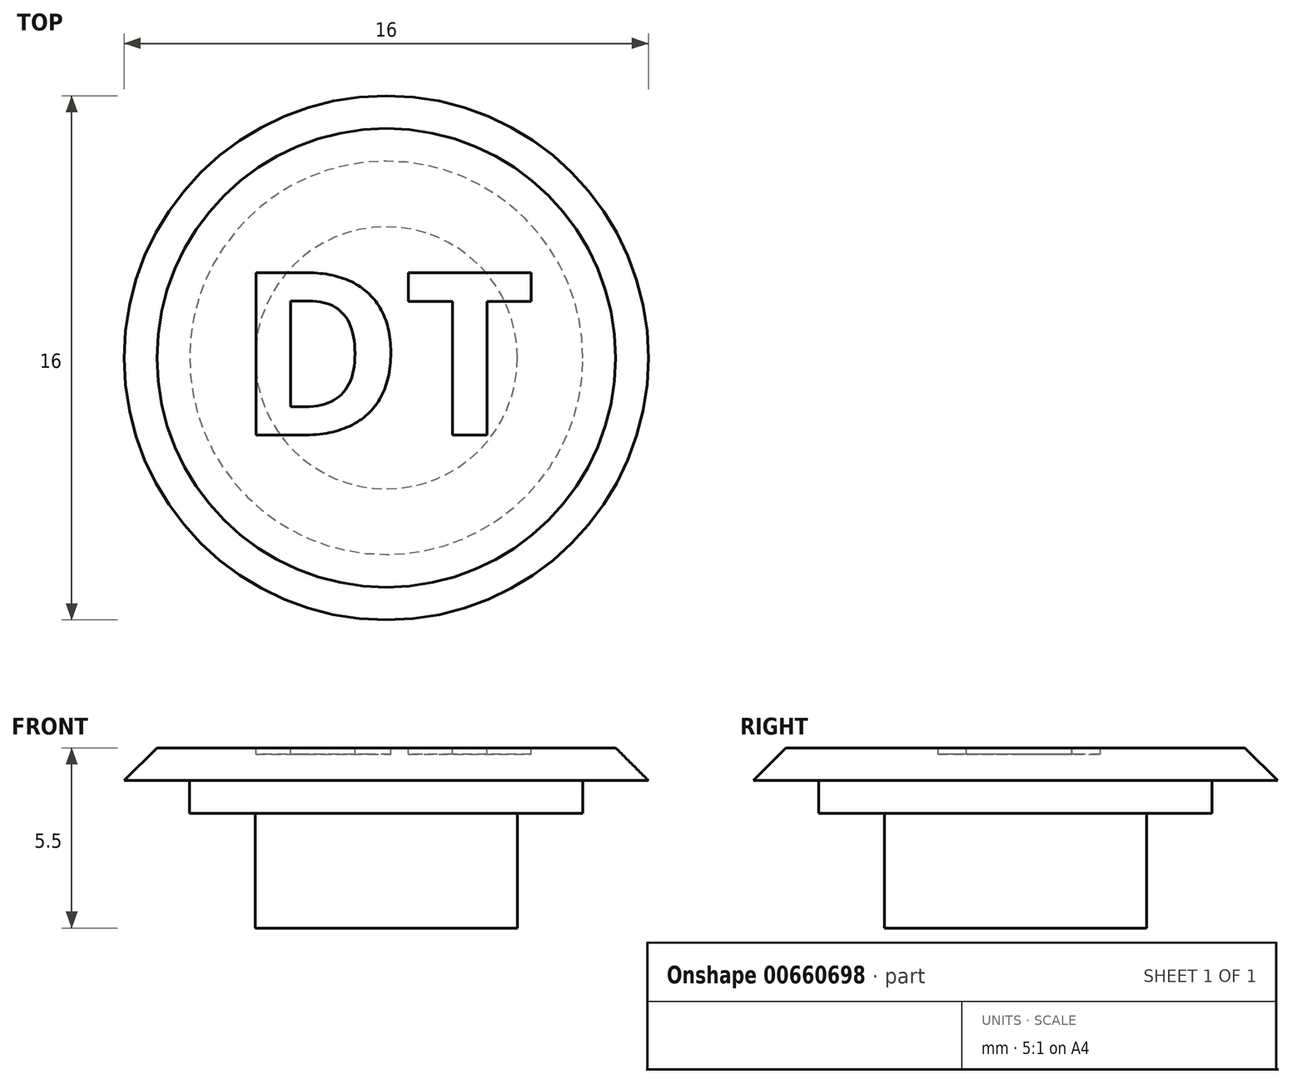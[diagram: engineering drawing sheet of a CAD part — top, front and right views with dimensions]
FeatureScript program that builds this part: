
annotation { "Feature Type Name" : "Feature", "Feature Type Description" : "" }
export const myFeature = defineFeature(function(context is Context, id is Id, definition is map)
    precondition{}
    {
        {
            var Q0;
            Q0=qCreatedBy(makeId("Top.planeOp"),FACE);
            var sketch = newSketch(context, id + "F0", { "sketchPlane" : qUnion([Q0])});
            skCircle(sketch, "E0", {"center": v(0, 0) * mm, "radius": 4 * mm});
            skSolve(sketch);
        }
        {
            var Q0;
            Q0=makeQuery(id+"F0.imprint","IMPRINT",FACE,{"disambiguationData":[TD([[makeQuery(id+"F0.imprint","IMPRINT",EDGE,{"derivedFrom":sQuery(id+"F0.wireOp",EDGE,"E0")}),1.0]])]});
            extrude(context, id + "F1", {"entities" : qUnion([Q0]), "depth" : 3.5 * mm, "offsetDistance" : 25 * mm});
        }
        {
            var Q0;
            Q0=makeQuery(id+"F1.opExtrude","CAP_FACE",FACE,{"disambiguationData":[OSD([sQuery(id+"F0.wireOp",EDGE,"E0")])],"isStart":false});
            var sketch = newSketch(context, id + "F2", { "sketchPlane" : qUnion([Q0])});
            skCircle(sketch, "E1", {"center": v(0, 0) * mm, "radius": 6 * mm});
            skSolve(sketch);
        }
        {
            var Q0;
            Q0=qSketchRegion(id+"F2",true);
            extrude(context, id + "F3", {"entities" : qUnion([Q0]), "operationType" : NewBodyOperationType.ADD, "depth" : 1 * mm, "offsetDistance" : 25 * mm});
        }
        {
            var Q0;
            Q0=makeQuery(id+"F3.opExtrude","CAP_FACE",FACE,{"disambiguationData":[OSD([sQuery(id+"F2.wireOp",EDGE,"E1")])],"isStart":false});
            var sketch = newSketch(context, id + "F4", { "sketchPlane" : qUnion([Q0])});
            skCircle(sketch, "E2", {"center": v(0, 0) * mm, "radius": 8 * mm});
            skSolve(sketch);
        }
        {
            var Q0;
            Q0=qSketchRegion(id+"F4",true);
            extrude(context, id + "F5", {"entities" : qUnion([Q0]), "operationType" : NewBodyOperationType.ADD, "depth" : 1 * mm, "offsetDistance" : 25 * mm});
        }
        {
            var Q0;
            Q0=makeQuery(id+"F5.opExtrude","CAP_FACE",FACE,{"disambiguationData":[OSD([sQuery(id+"F4.wireOp",EDGE,"E2")])],"isStart":false});
            var sketch = newSketch(context, id + "F6", { "sketchPlane" : qUnion([Q0])});
            skText(sketch, "E3", { "text": "DT", "fontName": "NotoSans-Bold.ttf"});
            const initialGuessF6  = {"E3": [-0.0046, -0.00236, 1, 0, 0.005]};
            skSetInitialGuess(sketch, initialGuessF6);
            skSolve(sketch);
        }
        {
            var Q0;
            Q0=makeQuery(id+"F6.imprint","IMPRINT",FACE,{"disambiguationData":[TD([[makeQuery(id+"F6.imprint","IMPRINT",EDGE,{"derivedFrom":sQuery(id+"F6.wireOp",EDGE,"E3.sketch_text.stroke-0")}),-1.0]])]});
            var Q1;
            Q1=makeQuery(id+"F6.imprint","IMPRINT",FACE,{"disambiguationData":[TD([[makeQuery(id+"F6.imprint","IMPRINT",EDGE,{"derivedFrom":sQuery(id+"F6.wireOp",EDGE,"E3.sketch_text.stroke-12")}),-1.0]])]});
            extrude(context, id + "F7", {"entities" : qUnion([Q0, Q1]), "operationType" : NewBodyOperationType.REMOVE, "oppositeDirection" : true, "depth" : 0.2 * mm, "offsetDistance" : 25 * mm});
        }
        {
            var Q0;
            Q0=makeQuery(id+"F5.opExtrude","CAP_EDGE",EDGE,{"disambiguationData":[OSD([sQuery(id+"F4.wireOp",EDGE,"E2")])],"isStart":false});
            chamfer(context, id + "F8", {"entities" : qUnion([Q0]), "width" : 1 * mm, "tangentPropagation" : true});
        }
    });
